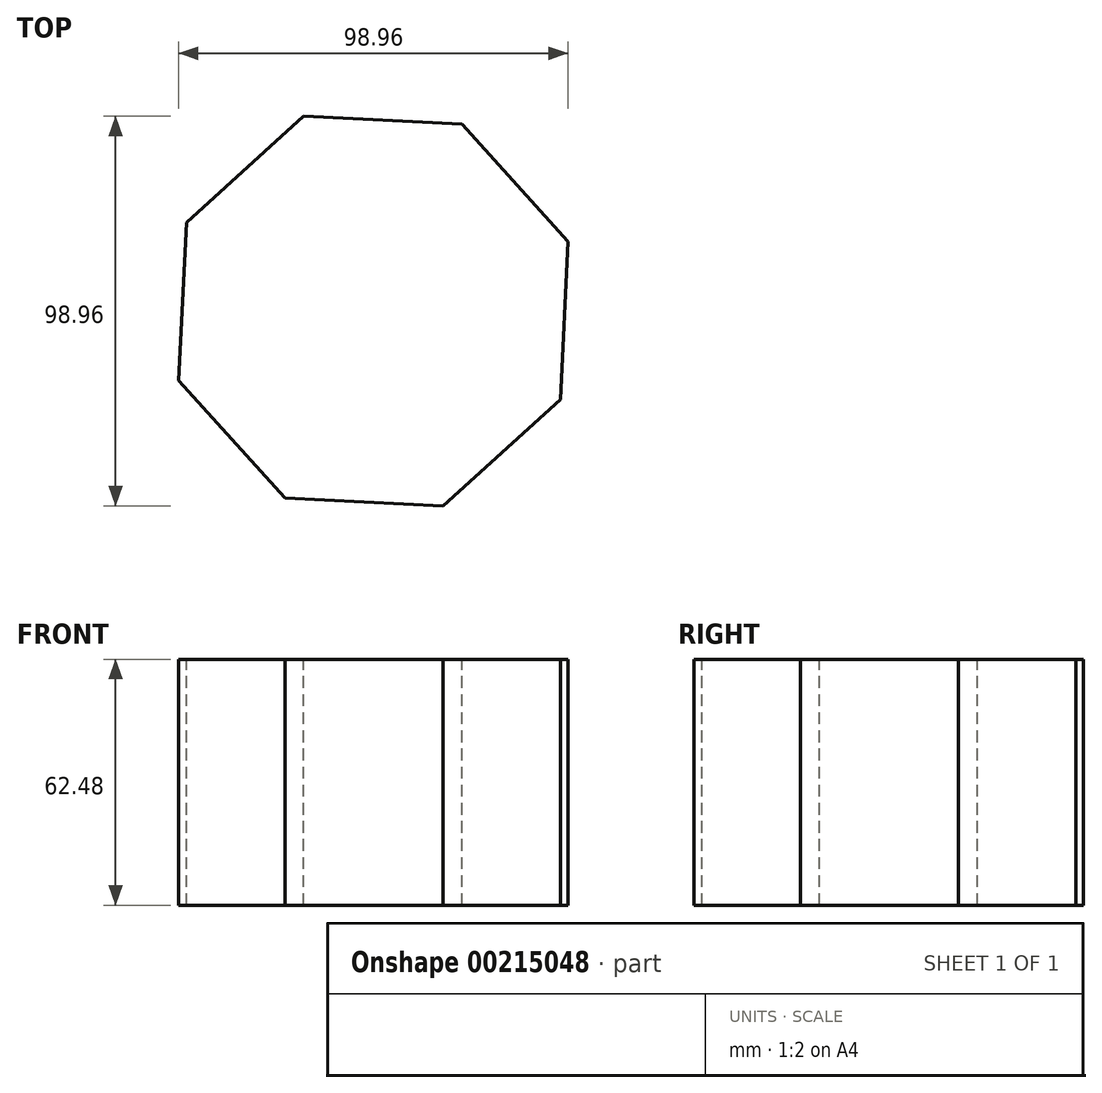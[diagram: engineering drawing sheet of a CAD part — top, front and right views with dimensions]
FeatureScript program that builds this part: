
annotation { "Feature Type Name" : "Feature", "Feature Type Description" : "" }
export const myFeature = defineFeature(function(context is Context, id is Id, definition is map)
    precondition{}
    {
        {
            var Q0;
            Q0=qCreatedBy(makeId("Top.planeOp"),FACE);
            var sketch = newSketch(context, id + "F0", { "sketchPlane" : qUnion([Q0])});
            skCircle(sketch, "E0.cCircle", {"center": v(0, 0) * mm, "radius": 48.54 * mm, "construction": true});
            skLineSegment(sketch, "E0.0", {"start": v(-47.48, 22.5) * mm, "end": v(-17.67, 49.48) * mm});
            skLineSegment(sketch, "E0.1", {"start": v(-17.67, 49.48) * mm, "end": v(22.5, 47.48) * mm});
            skLineSegment(sketch, "E0.2", {"start": v(22.5, 47.48) * mm, "end": v(49.48, 17.67) * mm});
            skLineSegment(sketch, "E0.3", {"start": v(49.48, 17.67) * mm, "end": v(47.48, -22.5) * mm});
            skLineSegment(sketch, "E0.4", {"start": v(47.48, -22.5) * mm, "end": v(17.67, -49.48) * mm});
            skLineSegment(sketch, "E0.5", {"start": v(17.67, -49.48) * mm, "end": v(-22.5, -47.48) * mm});
            skLineSegment(sketch, "E0.6", {"start": v(-22.5, -47.48) * mm, "end": v(-49.48, -17.67) * mm});
            skLineSegment(sketch, "E0.7", {"start": v(-49.48, -17.67) * mm, "end": v(-47.48, 22.5) * mm});
            skPoint(sketch, "E0.0.midPoint", {"position": v(-32.58, 35.98) * mm});
            skSolve(sketch);
        }
        {
            var Q0;
            Q0=makeQuery(id+"F0.imprint","IMPRINT",FACE,{"disambiguationData":[TD([[makeQuery(id+"F0.imprint","IMPRINT",EDGE,{"derivedFrom":sQuery(id+"F0.wireOp",EDGE,"E0.0")}),-1.0]])]});
            extrude(context, id + "F1", {"entities" : qUnion([Q0]), "oppositeDirection" : true, "depth" : 62.48 * mm});
        }
    });
